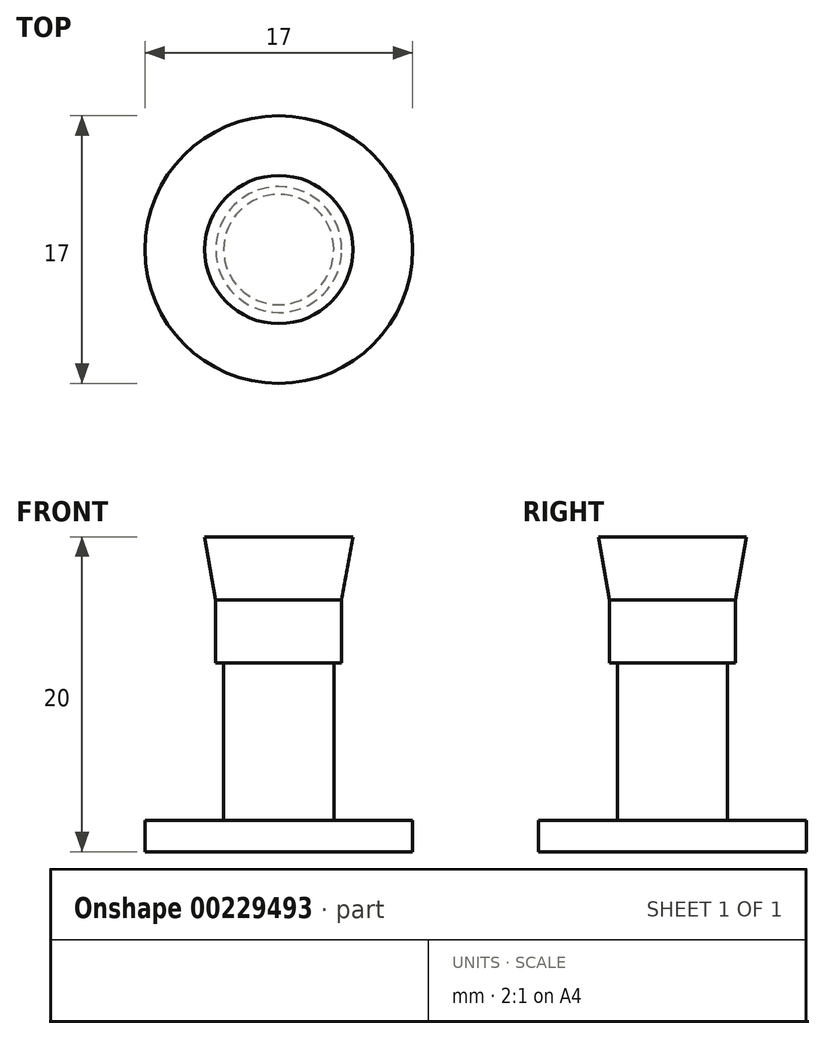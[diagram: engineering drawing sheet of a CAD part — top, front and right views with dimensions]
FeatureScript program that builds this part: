
annotation { "Feature Type Name" : "Feature", "Feature Type Description" : "" }
export const myFeature = defineFeature(function(context is Context, id is Id, definition is map)
    precondition{}
    {
        {
            var Q0;
            Q0=qCreatedBy(makeId("Top.planeOp"),FACE);
            var sketch = newSketch(context, id + "F0", { "sketchPlane" : qUnion([Q0])});
            skCircle(sketch, "E0", {"center": v(0, 0) * mm, "radius": 8.5 * mm});
            skSolve(sketch);
        }
        {
            var Q0;
            Q0 = qSketchRegion(id + "F0", true);
            extrude(context, id + "F1", {"entities" : qUnion([Q0]), "depth" : 2 * mm});
        }
        {
            var Q0;
            Q0=makeQuery(id+"F1.opExtrude","CAP_FACE",FACE,{"disambiguationData":[OSD([sQuery(id+"F0.wireOp",EDGE,"E0")])],"isStart":false});
            var sketch = newSketch(context, id + "F2", { "sketchPlane" : qUnion([Q0])});
            skCircle(sketch, "E1", {"center": v(0, 0) * mm, "radius": 3.5 * mm});
            skSolve(sketch);
        }
        {
            var Q0;
            Q0 = qSketchRegion(id + "F2", true);
            extrude(context, id + "F3", {"entities" : qUnion([Q0]), "operationType" : NewBodyOperationType.ADD, "depth" : 10 * mm});
        }
        {
            var Q0;
            Q0=makeQuery(id+"F3.opExtrude","CAP_FACE",FACE,{"disambiguationData":[OSD([sQuery(id+"F2.wireOp",EDGE,"E1")])],"isStart":false});
            var sketch = newSketch(context, id + "F4", { "sketchPlane" : qUnion([Q0])});
            skCircle(sketch, "E2", {"center": v(0, 0) * mm, "radius": 4 * mm});
            skSolve(sketch);
        }
        {
            var Q0;
            Q0 = qSketchRegion(id + "F4", true);
            extrude(context, id + "F5", {"entities" : qUnion([Q0]), "operationType" : NewBodyOperationType.ADD, "depth" : 4 * mm});
        }
        {
            var Q0;
            Q0=makeQuery(id+"F5.opExtrude","CAP_FACE",FACE,{"disambiguationData":[OSD([sQuery(id+"F4.wireOp",EDGE,"E2")])],"isStart":false});
            extrude(context, id + "F6", {"entities" : qUnion([Q0]), "operationType" : NewBodyOperationType.ADD, "depth" : 4 * mm, "hasDraft" : true, "draftAngle" : 10 * degree});
        }
    });
